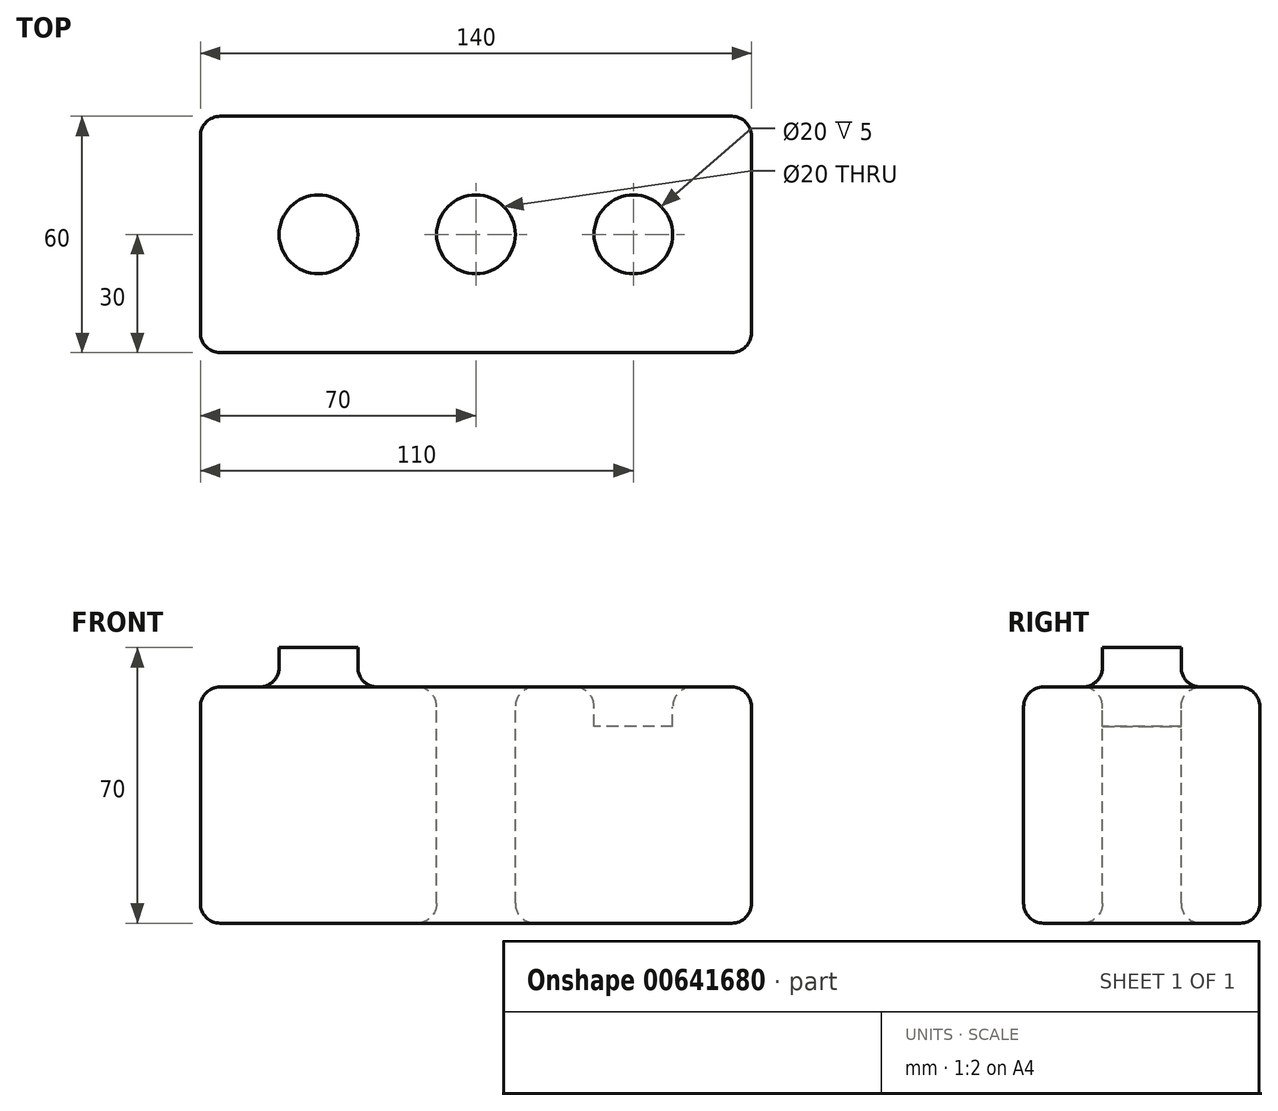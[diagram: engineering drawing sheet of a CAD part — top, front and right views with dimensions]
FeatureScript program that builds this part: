
annotation { "Feature Type Name" : "Feature", "Feature Type Description" : "" }
export const myFeature = defineFeature(function(context is Context, id is Id, definition is map)
    precondition{}
    {
        {
            var Q0;
            Q0=qCreatedBy(makeId("Top.planeOp"),FACE);
            var sketch = newSketch(context, id + "F0", { "sketchPlane" : qUnion([Q0])});
            skLineSegment(sketch, "E0.bottom", {"start": v(70, -30) * mm, "end": v(-70, -30) * mm});
            skLineSegment(sketch, "E0.top", {"start": v(70, 30) * mm, "end": v(-70, 30) * mm});
            skLineSegment(sketch, "E0.left", {"start": v(70, -30) * mm, "end": v(70, 30) * mm});
            skLineSegment(sketch, "E0.right", {"start": v(-70, -30) * mm, "end": v(-70, 30) * mm});
            skPoint(sketch, "E0.middle", {"position": v(0, 0) * mm});
            skSolve(sketch);
        }
        {
            var Q0;
            Q0 = qSketchRegion(id + "F0", true);
            extrude(context, id + "F1", {"entities" : qUnion([Q0]), "depth" : 60 * mm, "offsetDistance" : 25 * mm});
        }
        {
            var Q0;
            Q0=makeQuery(id+"F1.opExtrude","CAP_FACE",FACE,{"disambiguationData":[OSD([sQuery(id+"F0.wireOp",EDGE,"E0.bottom"),sQuery(id+"F0.wireOp",EDGE,"E0.top"),sQuery(id+"F0.wireOp",EDGE,"E0.left"),sQuery(id+"F0.wireOp",EDGE,"E0.right")])],"isStart":false});
            var sketch = newSketch(context, id + "F2", { "sketchPlane" : qUnion([Q0])});
            skCircle(sketch, "E1", {"center": v(-40, 0) * mm, "radius": 10 * mm});
            skSolve(sketch);
        }
        {
            var Q0;
            Q0=makeQuery(id+"F2.imprint","IMPRINT",FACE,{"disambiguationData":[TD([[makeQuery(id+"F2.imprint","IMPRINT",EDGE,{"derivedFrom":sQuery(id+"F2.wireOp",EDGE,"E1")}),-1.0]])]});
            var sketch = newSketch(context, id + "F3", { "sketchPlane" : qUnion([Q0])});
            skCircle(sketch, "E2", {"center": v(40, 0) * mm, "radius": 10 * mm});
            skSolve(sketch);
        }
        {
            var Q0;
            Q0=makeQuery(id+"F2.imprint","IMPRINT",FACE,{"disambiguationData":[TD([[makeQuery(id+"F2.imprint","IMPRINT",EDGE,{"derivedFrom":sQuery(id+"F2.wireOp",EDGE,"E1")}),-1.0]])]});
            var sketch = newSketch(context, id + "F4", { "sketchPlane" : qUnion([Q0])});
            skCircle(sketch, "E3", {"center": v(0, 0) * mm, "radius": 10 * mm});
            skSolve(sketch);
        }
        {
            var Q0;
            Q0=makeQuery(id+"F2.imprint","IMPRINT",FACE,{"disambiguationData":[TD([[makeQuery(id+"F2.imprint","IMPRINT",EDGE,{"derivedFrom":sQuery(id+"F2.wireOp",EDGE,"E1")}),1.0]])]});
            extrude(context, id + "F5", {"entities" : qUnion([Q0]), "operationType" : NewBodyOperationType.ADD, "depth" : 10 * mm, "offsetDistance" : 25 * mm});
        }
        {
            var Q0;
            Q0 = qSketchRegion(id + "F3", true);
            extrude(context, id + "F6", {"entities" : qUnion([Q0]), "operationType" : NewBodyOperationType.REMOVE, "oppositeDirection" : true, "depth" : 10 * mm, "offsetDistance" : 25 * mm});
        }
        {
            var Q0;
            Q0=makeQuery(id+"F4.imprint","IMPRINT",FACE,{"disambiguationData":[TD([[makeQuery(id+"F4.imprint","IMPRINT",EDGE,{"derivedFrom":sQuery(id+"F4.wireOp",EDGE,"E3")}),1.0]])]});
            extrude(context, id + "F7", {"entities" : qUnion([Q0]), "operationType" : NewBodyOperationType.REMOVE, "oppositeDirection" : true, "depth" : 132.8 * mm, "offsetDistance" : 25 * mm});
        }
        {
            var Q0;
            Q0=makeQuery(id+"F1.opExtrude","CAP_EDGE",EDGE,{"disambiguationData":[OSD([sQuery(id+"F0.wireOp",EDGE,"E0.right")])],"isStart":false});
            var Q1;
            Q1=makeQuery(id+"F1.opExtrude","CAP_EDGE",EDGE,{"disambiguationData":[OSD([sQuery(id+"F0.wireOp",EDGE,"E0.top")])],"isStart":false});
            var Q2;
            Q2=makeQuery(id+"F1.opExtrude","CAP_EDGE",EDGE,{"disambiguationData":[OSD([sQuery(id+"F0.wireOp",EDGE,"E0.bottom")])],"isStart":false});
            var Q3;
            Q3=makeQuery(id+"F1.opExtrude","CAP_FACE",FACE,{"disambiguationData":[OSD([sQuery(id+"F0.wireOp",EDGE,"E0.bottom"),sQuery(id+"F0.wireOp",EDGE,"E0.top"),sQuery(id+"F0.wireOp",EDGE,"E0.left"),sQuery(id+"F0.wireOp",EDGE,"E0.right")])],"isStart":false});
            var Q4;
            Q4=makeQuery(id+"F1.opExtrude","CAP_EDGE",EDGE,{"disambiguationData":[OSD([sQuery(id+"F0.wireOp",EDGE,"E0.top")])],"isStart":true});
            var Q5;
            Q5=makeQuery(id+"F1.opExtrude","SWEPT_EDGE",EDGE,{"disambiguationData":[OSD([sQuery(id+"F0.wireOp",EDGE,"E0.top"),sQuery(id+"F0.wireOp",EDGE,"E0.right")])]});
            var Q6;
            Q6=makeQuery(id+"F1.opExtrude","SWEPT_EDGE",EDGE,{"disambiguationData":[OSD([sQuery(id+"F0.wireOp",EDGE,"E0.top"),sQuery(id+"F0.wireOp",EDGE,"E0.left")])]});
            var Q7;
            Q7=makeQuery(id+"F1.opExtrude","SWEPT_EDGE",EDGE,{"disambiguationData":[OSD([sQuery(id+"F0.wireOp",EDGE,"E0.bottom"),sQuery(id+"F0.wireOp",EDGE,"E0.right")])]});
            var Q8;
            Q8=makeQuery(id+"F1.opExtrude","CAP_EDGE",EDGE,{"disambiguationData":[OSD([sQuery(id+"F0.wireOp",EDGE,"E0.right")])],"isStart":true});
            var Q9;
            Q9=makeQuery(id+"F1.opExtrude","CAP_EDGE",EDGE,{"disambiguationData":[OSD([sQuery(id+"F0.wireOp",EDGE,"E0.bottom")])],"isStart":true});
            var Q10;
            Q10=makeQuery(id+"F7.boolean.opBoolean","INTERSECT",EDGE,{"derivedFrom":[makeQuery(id+"F1.opExtrude","CAP_FACE",FACE,{"disambiguationData":[OSD([sQuery(id+"F0.wireOp",EDGE,"E0.bottom"),sQuery(id+"F0.wireOp",EDGE,"E0.top"),sQuery(id+"F0.wireOp",EDGE,"E0.left"),sQuery(id+"F0.wireOp",EDGE,"E0.right")])],"isStart":true}),makeQuery(id+"F7.opExtrude","SWEPT_FACE",FACE,{"disambiguationData":[OSD([sQuery(id+"F4.wireOp",EDGE,"E3")])]})]});
            var Q11;
            Q11=makeQuery(id+"F1.opExtrude","CAP_FACE",FACE,{"disambiguationData":[OSD([sQuery(id+"F0.wireOp",EDGE,"E0.bottom"),sQuery(id+"F0.wireOp",EDGE,"E0.top"),sQuery(id+"F0.wireOp",EDGE,"E0.left"),sQuery(id+"F0.wireOp",EDGE,"E0.right")])],"isStart":true});
            var Q12;
            Q12=makeQuery(id+"F1.opExtrude","SWEPT_EDGE",EDGE,{"disambiguationData":[OSD([sQuery(id+"F0.wireOp",EDGE,"E0.bottom"),sQuery(id+"F0.wireOp",EDGE,"E0.left")])]});
            fillet(context, id + "F8", {"entities" : qUnion([Q0, Q1, Q2, Q3, Q4, Q5, Q6, Q7, Q8, Q9, Q10, Q11, Q12]), "radius" : 5 * mm, "tangentPropagation" : true, "allowEdgeOverflow" : false});
        }
    });
